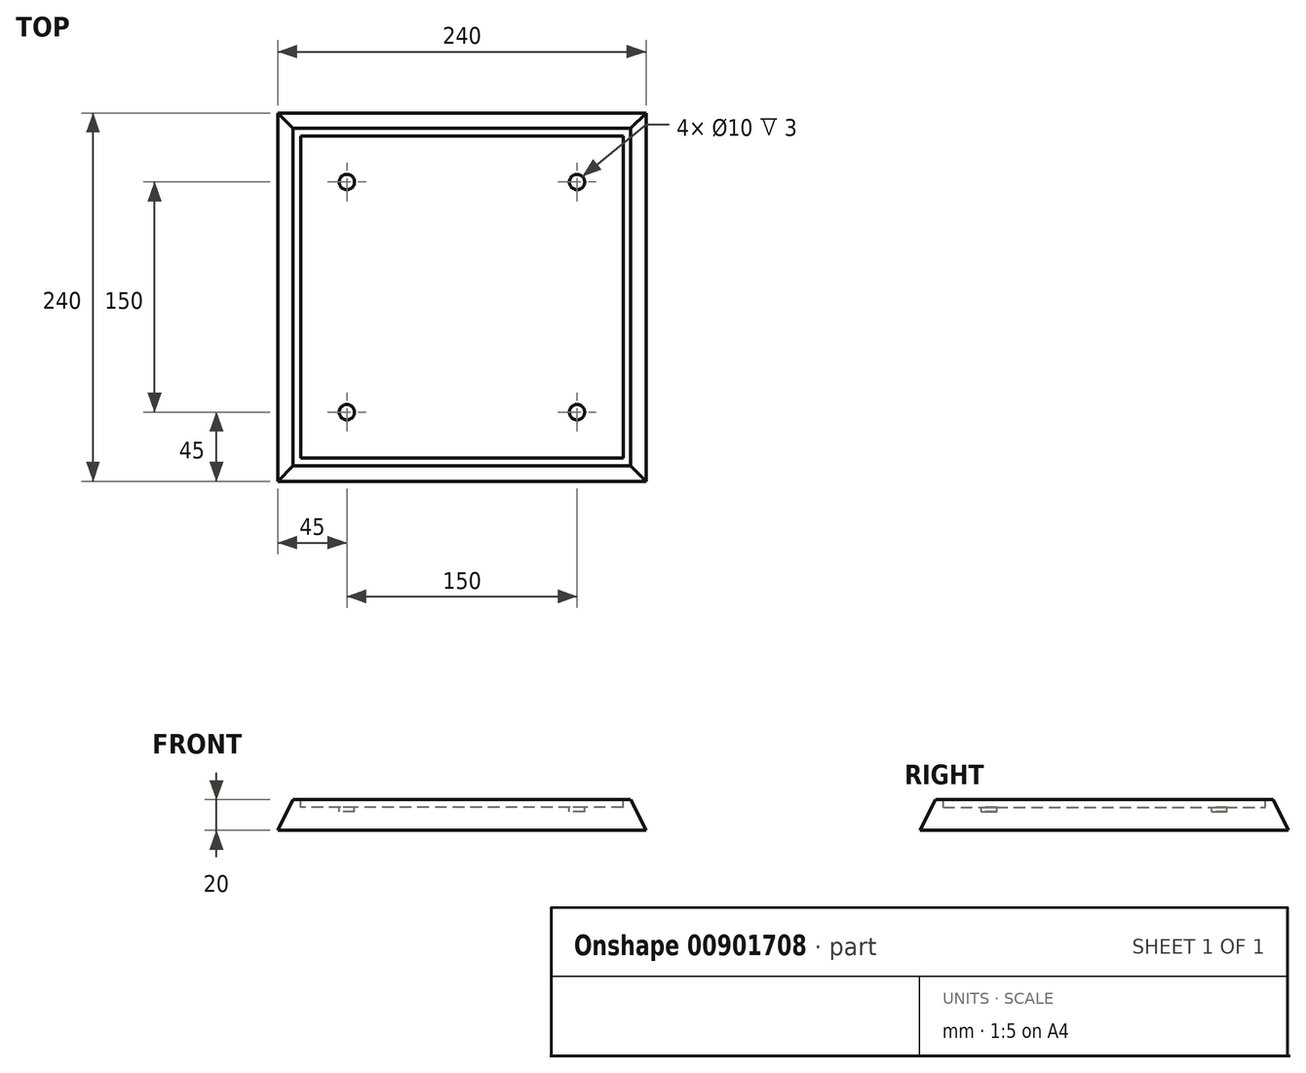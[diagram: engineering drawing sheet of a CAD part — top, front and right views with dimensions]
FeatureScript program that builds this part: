
annotation { "Feature Type Name" : "Feature", "Feature Type Description" : "" }
export const myFeature = defineFeature(function(context is Context, id is Id, definition is map)
    precondition{}
    {
        {
            var Q0;
            Q0=qCreatedBy(makeId("Top.planeOp"),FACE);
            var sketch = newSketch(context, id + "F0", { "sketchPlane" : qUnion([Q0])});
            skLineSegment(sketch, "E0.bottom", {"start": v(120, -120) * mm, "end": v(-120, -120) * mm});
            skLineSegment(sketch, "E0.top", {"start": v(120, 120) * mm, "end": v(-120, 120) * mm});
            skLineSegment(sketch, "E0.left", {"start": v(120, -120) * mm, "end": v(120, 120) * mm});
            skLineSegment(sketch, "E0.right", {"start": v(-120, -120) * mm, "end": v(-120, 120) * mm});
            skPoint(sketch, "E0.middle", {"position": v(0, 0) * mm});
            skSolve(sketch);
        }
        {
            var Q0;
            Q0=makeQuery(id+"F0.imprint","IMPRINT",FACE,{"disambiguationData":[TD([[makeQuery(id+"F0.imprint","IMPRINT",EDGE,{"derivedFrom":sQuery(id+"F0.wireOp",EDGE,"E0.bottom")}),-1.0]])]});
            cPlane(context, id + "F1", {"entities" : qUnion([Q0]), "cplaneType" : CPlaneType.OFFSET, "offset" : 20 * mm, "width" : 150 * mm, "height" : 150 * mm});
        }
        {
            var Q0;
            Q0=qCreatedBy(id+"F1.planeOp",FACE);
            var sketch = newSketch(context, id + "F2", { "sketchPlane" : qUnion([Q0])});
            skLineSegment(sketch, "E1.bottom", {"start": v(110, -110) * mm, "end": v(-110, -110) * mm});
            skLineSegment(sketch, "E1.top", {"start": v(110, 110) * mm, "end": v(-110, 110) * mm});
            skLineSegment(sketch, "E1.left", {"start": v(110, -110) * mm, "end": v(110, 110) * mm});
            skLineSegment(sketch, "E1.right", {"start": v(-110, -110) * mm, "end": v(-110, 110) * mm});
            skPoint(sketch, "E1.middle", {"position": v(0, 0) * mm});
            skSolve(sketch);
        }
        {
            var Q0;
            Q0=makeQuery(id+"F0.imprint","IMPRINT",FACE,{"disambiguationData":[TD([[makeQuery(id+"F0.imprint","IMPRINT",EDGE,{"derivedFrom":sQuery(id+"F0.wireOp",EDGE,"E0.bottom")}),-1.0]])]});
            var Q1;
            Q1=makeQuery(id+"F2.imprint","IMPRINT",FACE,{"disambiguationData":[TD([[makeQuery(id+"F2.imprint","IMPRINT",EDGE,{"derivedFrom":sQuery(id+"F2.wireOp",EDGE,"E1.bottom")}),-1.0]])]});
            loft(context, id + "F3", {"sheetProfilesArray" : [{ "sheetProfileEntities" : qUnion([Q0]) }, { "sheetProfileEntities" : qUnion([Q1]) }]});
        }
        {
            var Q0;
            Q0=makeQuery(id+"F3.opLoft","CAP_FACE",FACE,{"disambiguationData":[OSD([makeQuery(id+"F2.imprint","IMPRINT",FACE,{"disambiguationData":[TD([[makeQuery(id+"F2.imprint","IMPRINT",EDGE,{"derivedFrom":sQuery(id+"F2.wireOp",EDGE,"E1.bottom")}),-1.0]])]})])],"isStart":true});
            var sketch = newSketch(context, id + "F4", { "sketchPlane" : qUnion([Q0])});
            skLineSegment(sketch, "E2.bottom", {"start": v(105, -105) * mm, "end": v(-105, -105) * mm});
            skLineSegment(sketch, "E2.top", {"start": v(105, 105) * mm, "end": v(-105, 105) * mm});
            skLineSegment(sketch, "E2.left", {"start": v(105, -105) * mm, "end": v(105, 105) * mm});
            skLineSegment(sketch, "E2.right", {"start": v(-105, -105) * mm, "end": v(-105, 105) * mm});
            skPoint(sketch, "E2.middle", {"position": v(0, 0) * mm});
            skSolve(sketch);
        }
        {
            var Q0;
            Q0=makeQuery(id+"F4.imprint","IMPRINT",FACE,{"disambiguationData":[TD([[makeQuery(id+"F4.imprint","IMPRINT",EDGE,{"derivedFrom":sQuery(id+"F4.wireOp",EDGE,"E2.bottom")}),-1.0]])]});
            extrude(context, id + "F5", {"entities" : qUnion([Q0]), "operationType" : NewBodyOperationType.REMOVE, "oppositeDirection" : true, "depth" : 5 * mm, "offsetDistance" : 25 * mm});
        }
        {
            var Q0;
            Q0=makeQuery(id+"F5.boolean.opBoolean","COPY",FACE,{"derivedFrom":makeQuery(id+"F5.opExtrude","CAP_FACE",FACE,{"disambiguationData":[OSD([sQuery(id+"F4.wireOp",EDGE,"E2.bottom"),sQuery(id+"F4.wireOp",EDGE,"E2.top"),sQuery(id+"F4.wireOp",EDGE,"E2.left"),sQuery(id+"F4.wireOp",EDGE,"E2.right")])],"isStart":false})});
            var sketch = newSketch(context, id + "F6", { "sketchPlane" : qUnion([Q0])});
            skLineSegment(sketch, "E3.bottom", {"start": v(75, -75) * mm, "end": v(-75, -75) * mm});
            skLineSegment(sketch, "E3.top", {"start": v(75, 75) * mm, "end": v(-75, 75) * mm});
            skLineSegment(sketch, "E3.left", {"start": v(75, -75) * mm, "end": v(75, 75) * mm});
            skLineSegment(sketch, "E3.right", {"start": v(-75, -75) * mm, "end": v(-75, 75) * mm});
            skPoint(sketch, "E3.middle", {"position": v(0, 0) * mm});
            skCircle(sketch, "E4", {"center": v(-75, 75) * mm, "radius": 5 * mm});
            skCircle(sketch, "E5", {"center": v(75, 75) * mm, "radius": 5 * mm});
            skCircle(sketch, "E6", {"center": v(75, -75) * mm, "radius": 5 * mm});
            skCircle(sketch, "E7", {"center": v(-75, -75) * mm, "radius": 5 * mm});
            skSolve(sketch);
        }
        {
            var Q0;
            {var subQ0=sQuery(id+"F6.wireOp",EDGE,"E3.right");var subQ1=sQuery(id+"F6.wireOp",EDGE,"E3.top");var subQ2=makeQuery(id+"F6.imprint","INTERSECT",VERTEX,{"derivedFrom":[subQ1,subQ0]});Q0=makeQuery(id+"F6.imprint","IMPRINT",FACE,{"disambiguationData":[TD([[makeQuery(id+"F6.imprint","IMPRINT",EDGE,{"disambiguationData":[TD([[subQ2,1.0]])],"derivedFrom":subQ1}),-1.0]])]});}
            var Q1;
            {var subQ0=sQuery(id+"F6.wireOp",EDGE,"E3.right");var subQ1=sQuery(id+"F6.wireOp",EDGE,"E3.top");var subQ2=makeQuery(id+"F6.imprint","INTERSECT",VERTEX,{"derivedFrom":[subQ1,subQ0]});Q1=makeQuery(id+"F6.imprint","IMPRINT",FACE,{"disambiguationData":[TD([[makeQuery(id+"F6.imprint","IMPRINT",EDGE,{"disambiguationData":[TD([[subQ2,1.0]])],"derivedFrom":subQ1}),1.0]])]});}
            var Q2;
            {var subQ0=sQuery(id+"F6.wireOp",EDGE,"E3.left");var subQ1=sQuery(id+"F6.wireOp",EDGE,"E3.top");var subQ2=makeQuery(id+"F6.imprint","INTERSECT",VERTEX,{"derivedFrom":[subQ1,subQ0]});Q2=makeQuery(id+"F6.imprint","IMPRINT",FACE,{"disambiguationData":[TD([[makeQuery(id+"F6.imprint","IMPRINT",EDGE,{"disambiguationData":[TD([[subQ2,-1.0]])],"derivedFrom":subQ1}),1.0]])]});}
            var Q3;
            {var subQ0=sQuery(id+"F6.wireOp",EDGE,"E3.left");var subQ1=sQuery(id+"F6.wireOp",EDGE,"E3.top");var subQ2=makeQuery(id+"F6.imprint","INTERSECT",VERTEX,{"derivedFrom":[subQ1,subQ0]});Q3=makeQuery(id+"F6.imprint","IMPRINT",FACE,{"disambiguationData":[TD([[makeQuery(id+"F6.imprint","IMPRINT",EDGE,{"disambiguationData":[TD([[subQ2,-1.0]])],"derivedFrom":subQ1}),-1.0]])]});}
            var Q4;
            {var subQ0=sQuery(id+"F6.wireOp",EDGE,"E3.left");var subQ1=sQuery(id+"F6.wireOp",EDGE,"E3.bottom");var subQ2=makeQuery(id+"F6.imprint","INTERSECT",VERTEX,{"derivedFrom":[subQ1,subQ0]});Q4=makeQuery(id+"F6.imprint","IMPRINT",FACE,{"disambiguationData":[TD([[makeQuery(id+"F6.imprint","IMPRINT",EDGE,{"disambiguationData":[TD([[subQ2,-1.0]])],"derivedFrom":subQ1}),-1.0]])]});}
            var Q5;
            {var subQ0=sQuery(id+"F6.wireOp",EDGE,"E3.left");var subQ1=sQuery(id+"F6.wireOp",EDGE,"E3.bottom");var subQ2=makeQuery(id+"F6.imprint","INTERSECT",VERTEX,{"derivedFrom":[subQ1,subQ0]});Q5=makeQuery(id+"F6.imprint","IMPRINT",FACE,{"disambiguationData":[TD([[makeQuery(id+"F6.imprint","IMPRINT",EDGE,{"disambiguationData":[TD([[subQ2,-1.0]])],"derivedFrom":subQ1}),1.0]])]});}
            var Q6;
            {var subQ0=sQuery(id+"F6.wireOp",EDGE,"E3.right");var subQ1=sQuery(id+"F6.wireOp",EDGE,"E3.bottom");var subQ2=makeQuery(id+"F6.imprint","INTERSECT",VERTEX,{"derivedFrom":[subQ1,subQ0]});Q6=makeQuery(id+"F6.imprint","IMPRINT",FACE,{"disambiguationData":[TD([[makeQuery(id+"F6.imprint","IMPRINT",EDGE,{"disambiguationData":[TD([[subQ2,1.0]])],"derivedFrom":subQ1}),-1.0]])]});}
            var Q7;
            {var subQ0=sQuery(id+"F6.wireOp",EDGE,"E3.right");var subQ1=sQuery(id+"F6.wireOp",EDGE,"E3.bottom");var subQ2=makeQuery(id+"F6.imprint","INTERSECT",VERTEX,{"derivedFrom":[subQ1,subQ0]});Q7=makeQuery(id+"F6.imprint","IMPRINT",FACE,{"disambiguationData":[TD([[makeQuery(id+"F6.imprint","IMPRINT",EDGE,{"disambiguationData":[TD([[subQ2,1.0]])],"derivedFrom":subQ1}),1.0]])]});}
            extrude(context, id + "F7", {"entities" : qUnion([Q0, Q1, Q2, Q3, Q4, Q5, Q6, Q7]), "operationType" : NewBodyOperationType.REMOVE, "oppositeDirection" : true, "depth" : 3 * mm, "offsetDistance" : 25 * mm});
        }
    });
